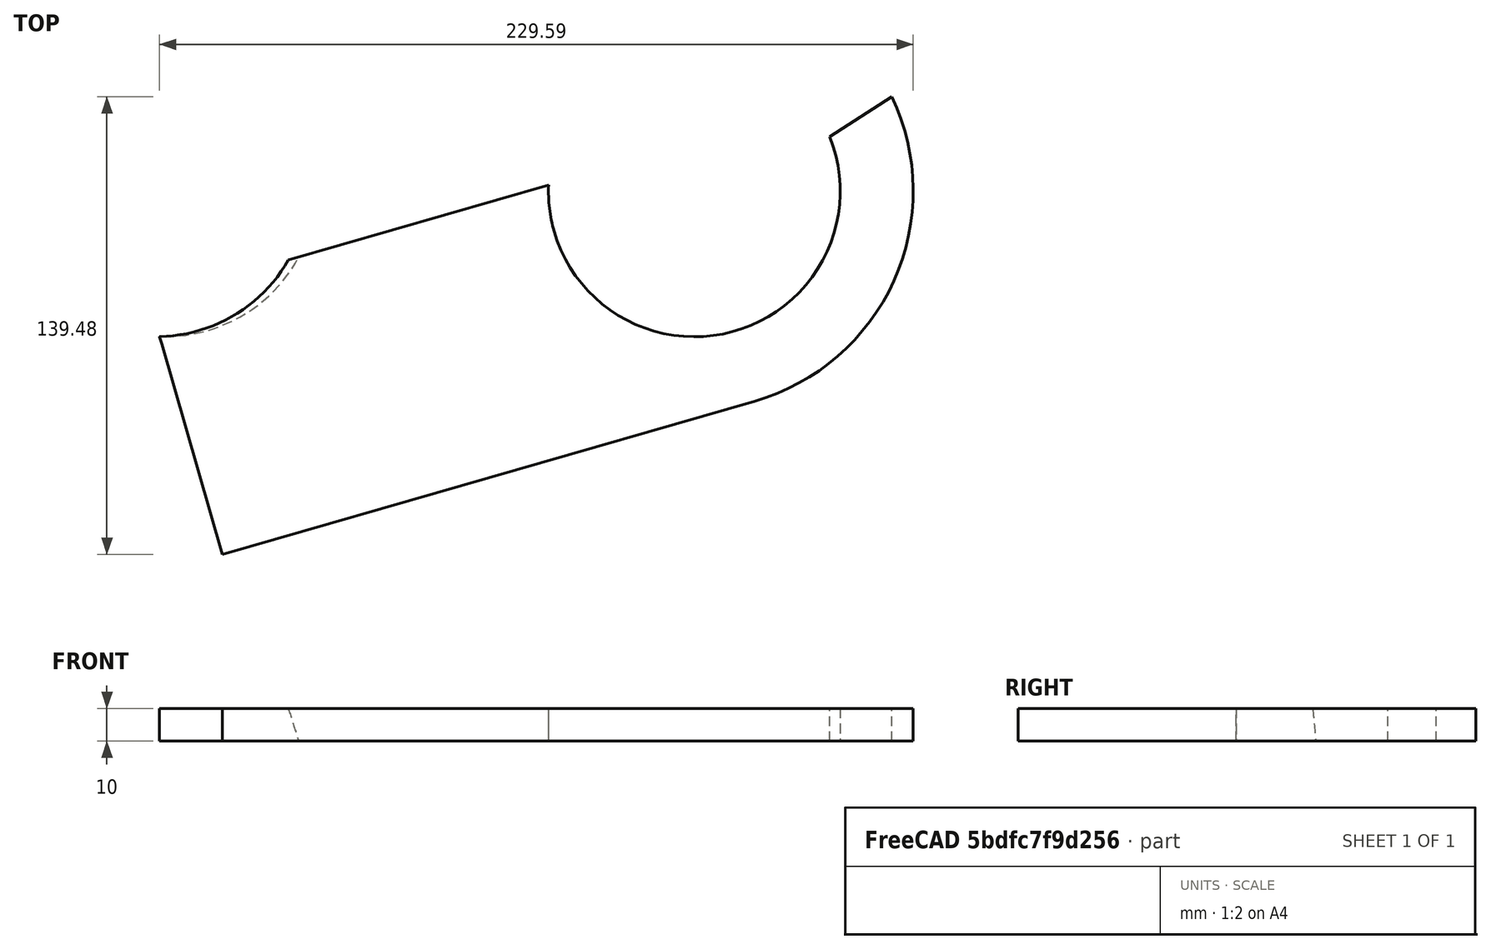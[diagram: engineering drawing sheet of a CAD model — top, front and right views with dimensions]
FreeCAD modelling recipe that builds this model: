
FCSTD DOCUMENT  (FreeCAD 1.0R39109 (Git))
Label: Tail_Hinge_Outer
License: All rights reserved
LicenseURL: http://en.wikipedia.org/wiki/All_rights_reserved
objects: App::Link×3, Spreadsheet::Sheet×1, Part::Cylinder×1, Part::Cut×1, App::Part×1
note: 2 computed .brp shape members not serialized (recipe doc carries the construction recipe); baked Part::Feature solids carry a one-line shape summary decoded from their .brp
EXTERNAL_REF file=Tail_Hinge_Outer_Pipe.FCStd obj=Tube
EXTERNAL_REF file=Tail_Hinge_Outer_Pipe_Cover.FCStd obj=PadBody
EXTERNAL_REF file=../../../Master_of_Puppets.FCStd obj=Alternator
EXTERNAL_REF file=../../../Master_of_Puppets.FCStd obj=HighEndStop
EXTERNAL_REF file=../../../Master_of_Puppets.FCStd obj=LowEndStop
EXTERNAL_REF file=../../../Master_of_Puppets.FCStd obj=Spreadsheet
EXTERNAL_REF file=../../../Master_of_Puppets.FCStd obj=Tail
EXTERNAL_REF file=../../Stops/Tail_Stop_LowEnd.FCStd obj=PocketBody

FEATURE [App::Link] Link  label="Pipe"
  LinkedObject = -> <external Tail_Hinge_Outer_Pipe.FCStd>#Tube
FEATURE [App::Link] Link001  label="Outer_Pipe_Cover"
  LinkPlacement = pos=(0,0,225.987) rot=(0,0,1;0rad)
  LinkedObject = -> <external Tail_Hinge_Outer_Pipe_Cover.FCStd>#PadBody
  Placement = pos=(0,0,225.987) rot=(0,0,1;0rad)
  expr: .Placement.Base.z = Spreadsheet.HingeOuterPipeCoverZ
FEATURE [Spreadsheet::Sheet] Spreadsheet
  cells = A1='Inputs; A2='HingeOuterPipeLength; B2(HingeOuterPipeLength)==Master_of_Puppets#Tail.HingeOuterPipeLength; A3='FlatMetalThickness; B3(FlatMetalThickness)==Master_of_Puppets#Spreadsheet.FlatMetalThickness; A4='TailBoomTriangularBraceWidth; B4(TailBoomTriangularBraceWidth)==Master_of_Puppets#Tail.TailBoomTriangularBraceWidth; A5='LowEndStopPlacement; B5(LowEndStopPlacement)==Master_of_Puppets#LowEndStop.LowEndStopPlacement; A6='YawPipeRadius; B6(YawPipeRadius)==Master_of_Puppets#Alternator.YawPipeRadius; A7='YawPipeLength; B7(YawPipeLength)==Master_of_Puppets#HighEndStop.YawPipeLength; A8='OuterTailHingePlacement; B8(OuterTailHingePlacement)==Master_of_Puppets#Tail.OuterTailHingePlacement; A9='TailAssemblyPlacement; B9(TailAssemblyPlacement)==Master_of_Puppets#HighEndStop.TailAssemblyPlacement; A10='Placement; A11='HingeOuterPipeCoverZ; B11(HingeOuterPipeCoverZ)==HingeOuterPipeLength; A12='YawBearingCylinderPlacement; B12(YawBearingCylinderPlacement)==minvert(OuterTailHingePlacement) * minvert(TailAssemblyPlacement)
FEATURE [App::Link] Link002  label="Stop_LowEnd"
  LinkPlacement = pos=(0,0,155.983) rot=(0,0,-1;1.29045rad)
  LinkedObject = -> <external ../../Stops/Tail_Stop_LowEnd.FCStd>#PocketBody
  Placement = pos=(0,0,155.983) rot=(0,0,-1;1.29045rad)
  expr: Placement = Spreadsheet.LowEndStopPlacement
FEATURE [Part::Cylinder] Cylinder  label="YawBearing_Cylinder"
  Angle = 360
  AttacherType = Attacher::AttachEngine3D
  FirstAngle = 0
  Height = 405
  Placement = pos=(-79.4354,1.24e-14,-150.518) rot=(-0.130416,-0.04112,0.990606;2.53612rad)
  Radius = 44.45
  SecondAngle = 0
  expr: Height = Spreadsheet.YawPipeLength
  expr: Placement = Spreadsheet.YawBearingCylinderPlacement
  expr: Radius = Spreadsheet.YawPipeRadius
FEATURE [Part::Cut] Cut  label="Tail_Stop_LowEnd"
  Base = -> Link002
  Openafpm_Flat = true
  Tool = -> Cylinder
FEATURE [App::Part] Part  label="Tail_Hinge_Outer"
  Group = -> [Link,Link001,Link002,Cylinder,Cut]
  Origin = -> Origin

RESOLVED EXTERNAL PARTS (link-assembly join: the EXTERNAL_REF files above that resolve inside this repo's crawl, each included once):
---- part ../../../Master_of_Puppets.FCStd = doc fcstd_6404554055c4 (61625 chars; too large to inline — full recipe in that document) ----
---- part ../../Stops/Tail_Stop_LowEnd.FCStd = doc fcstd_18032a887a06 ----
FCSTD DOCUMENT  (FreeCAD 0.21R33675 (Git))
Label: Tail_Stop_LowEnd
License: All rights reserved
LicenseURL: http://en.wikipedia.org/wiki/All_rights_reserved
objects: Sketcher::SketchObject×1, PartDesign::Pad×1, Spreadsheet::Sheet×1, PartDesign::Body×1
note: 4 computed .brp shape members not serialized (recipe doc carries the construction recipe); baked Part::Feature solids carry a one-line shape summary decoded from their .brp
EXTERNAL_REF file=../../Master_of_Puppets.FCStd obj=LowEndStop
EXTERNAL_REF file=../../Master_of_Puppets.FCStd obj=Spreadsheet
EXTERNAL_REF file=../../Master_of_Puppets.FCStd obj=Tail

FEATURE [Sketcher::SketchObject] Sketch
  FullyConstrained = true
  MapMode = 5
  Support = -> [XY_Plane001]
  expr: Constraints[13] = Spreadsheet.InnerArcAngle
  expr: Constraints[14] = Spreadsheet.OuterArcAngle
  expr: Constraints[15] = Spreadsheet.LowEndStopWidth
  expr: Constraints[1] = Spreadsheet.LowEndStopLength
  expr: Constraints[24] = Spreadsheet.LowEndStopWidth
  expr: Constraints[25] = Spreadsheet.LowEndStopLength
  expr: Constraints[33] = Spreadsheet.LowEndStopYawBearingOverlap
  expr: Constraints[7] = Spreadsheet.HingeOuterPipeRadius
  sketch-geometry (12):
    g0: LineSegment StartX=0 StartY=0 StartZ=0 EndX=0 EndY=-198.64 EndZ=0
    g1: LineSegment StartX=66.675 StartY=-198.64 StartZ=0 EndX=66.675 EndY=0 EndZ=0
    g2: ArcOfCircle CenterX=0 CenterY=0 CenterZ=0 NormalX=0 NormalY=0 NormalZ=1 AngleXU=0 Radius=66.675 StartAngle=0 EndAngle=1.48304
    g3: Circle CenterX=0 CenterY=0 CenterZ=0 NormalX=0 NormalY=0 NormalZ=1 AngleXU=0 Radius=44.45
    g4: ArcOfCircle CenterX=0 CenterY=0 CenterZ=0 NormalX=0 NormalY=0 NormalZ=1 AngleXU=0 Radius=44.45 StartAngle=4.71239 EndAngle=7.71269
    g5: LineSegment StartX=6.25936 StartY=44.0071 StartZ=0 EndX=5.84395 EndY=66.4184 EndZ=0
    g6: LineSegment StartX=-8.2e-15 StartY=-198.64 StartZ=0 EndX=-8.2e-15 EndY=-44.45 EndZ=0
    g7: ArcOfCircle CenterX=0 CenterY=0 CenterZ=0 NormalX=0 NormalY=0 NormalZ=1 AngleXU=0 Radius=44.45 StartAngle=4.71239 EndAngle=10.9956
    g8: LineSegment StartX=-8.2e-15 StartY=-198.64 StartZ=0 EndX=66.675 EndY=-198.64 EndZ=0
    g9: LineSegment StartX=-8.2e-15 StartY=-198.64 StartZ=0 EndX=-14 EndY=-198.64 EndZ=0
    g10: LineSegment StartX=-14 StartY=-198.64 StartZ=0 EndX=-14 EndY=-42.1877 EndZ=0
    g11: ArcOfCircle CenterX=0 CenterY=0 CenterZ=0 NormalX=0 NormalY=0 NormalZ=1 AngleXU=0 Radius=44.45 StartAngle=4.39197 EndAngle=4.71239
  constraints (34):
    c: Vertical(g1)
    c: Distance(g0) = 198.64
    c: Coincident(g0,g-1)
    c: Coincident(g2,g0)
    c: Coincident(g2,g1)
    c: PointOnObject(g1,g-1)
    c: Coincident(g3,g2)
    c: Radius(g3) = 44.45
    c: PointOnObject(g4,g0)
    c: Coincident(g4,g2)
    c: PointOnObject(g4,g3)
    c: Coincident(g5,g4)
    c: Coincident(g5,g2)
    c: Angle(g4) = 3.00031
    c: Angle(g2) = 1.48304
    c: DistanceX(g-2,g1) = 66.675
    c: Vertical(g6)
    c: Vertical(g0)
    c: Coincident(g7,g2)
    c: Coincident(g7,g4)
    c: Coincident(g7,g6)
    c: Coincident(g8,g6)
    c: Coincident(g8,g1)
    c: Horizontal(g8)
    c: DistanceX(g8,g8) = 66.675
    c: DistanceY(g6,g2) = 198.64
    c: Coincident(g9,g6)
    c: Horizontal(g9)
    c: Coincident(g10,g9)
    c: Vertical(g10)
    c: Coincident(g11,g2)
    c: Coincident(g11,g4)
    c: Coincident(g11,g10)
    c: DistanceX(g9,g9) = 14
FEATURE [PartDesign::Pad] Pad
  AllowMultiFace = false
  Direction = (0,0,1)
  Length = 10
  Length2 = 100
  Profile = -> Sketch
  Type = 0
  expr: Length = Spreadsheet.FlatMetalThickness
FEATURE [Spreadsheet::Sheet] Spreadsheet
  cells = A1='Inputs; A2='YawPipeDiameter; B2(YawPipeDiameter)==Master_of_Puppets#Spreadsheet.YawPipeDiameter; A3='FlatMetalThickness; B3(FlatMetalThickness)==Master_of_Puppets#Spreadsheet.FlatMetalThickness; A4='TailHingeJunctionFullWidth; B4(TailHingeJunctionFullWidth)==Master_of_Puppets#Tail.TailHingeJunctionFullWidth; A5='OuterTailHingeLowEndStopAngle; B5(OuterTailHingeLowEndStopAngle)==Master_of_Puppets#LowEndStop.LowEndStopAngle; A6='TailBoomTriangularBraceWidth; B6(TailBoomTriangularBraceWidth)==Master_of_Puppets#Tail.TailBoomTriangularBraceWidth; A7='TailAngle; B7(TailAngle)==Master_of_Puppets#Tail.TailAngle; A8='TailY; B8(TailBoomY)==Master_of_Puppets#Tail.TailY; A9='LowEndStopLength; B9(LowEndStopLength)==Master_of_Puppets#LowEndStop.LowEndStopLength; A10='RotorDiskRadius; B10(RotorDiskRadius)==Master_of_Puppets#Spreadsheet.RotorDiskRadius; A11='OuterLowEndStopWidth; B11(OuterLowEndStopWidth)==Master_of_Puppets#LowEndStop.OuterLowEndStopWidth; A12='LowEndStopYawBearingOverlap; B12(LowEndStopYawBearingOverlap)==Master_of_Puppets#LowEndStop.LowEndStopYawBearingOverlap; A13='LowEndStopWidth; B13(LowEndStopWidth)==Master_of_Puppets#LowEndStop.LowEndStopWidth; A14='HingeOuterPipeRadius; B14(HingeOuterPipeRadius)==Master_of_Puppets#Tail.HingeOuterPipeRadius; A15='Calculated; A16='HalfTriangularBraceThickness; B16(HalfTriangularBraceThickness)==FlatMetalThickness / 2; A17='TriangularBraceOffsetFactor; B17(TriangularBraceOffsetFactor)=-1; C17='Set TriangularBraceOffsetFactor to 1 to extend low end stop underneath boom & above boom support; A18='Inner Arc Angle; C18='Outer Arc Angle; A19='InnerTriangularBraceAngleOffset; B19(InnerTriangularBraceAngleOffset)==HalfTriangularBraceThickness / HingeOuterPipeRadius * 180 / pi * 1 deg * TriangularBraceOffsetFactor; C19='OuterTriangularBraceAngleOffset; D19(OuterTriangularBraceAngleOffset)==HalfTriangularBraceThickness / LowEndStopWidth * 180 / pi * 1 deg * TriangularBraceOffsetFactor; A20='InnerTailBoomYAngleOffset; B20(InnerTailBoomYAngleOffset)==TailBoomY / HingeOuterPipeRadius * 180 / pi * 1 deg; C20='OuterTailBoomYAngleOffset; D20(OuterTailBoomYAngleOffset)==TailBoomY / LowEndStopWidth * 180 / pi * 1 deg; C21='TailBoomRotationYOffset; D21(TailBoomRotationYOffset)==sin(TailAngle) * OuterLowEndStopWidth; A22='InnerAngle; B22(InnerAngle)==OuterTailHingeLowEndStopAngle + InnerTriangularBraceAngleOffset + InnerTailBoomYAngleOffset; C22='TailBoomRotationAngleOffset; D22(TailBoomRotationAngleOffset)==TailBoomRotationYOffset / LowEndStopWidth * 180 / pi * 1 deg; A23='InnerArcAngle; B23(InnerArcAngle)==90 deg + InnerAngle; C23='OuterArcAngle; D23(OuterArcAngle)==OuterTailHingeLowEndStopAngle + OuterTriangularBraceAngleOffset + OuterTailBoomYAngleOffset + TailBoomRotationAngleOffset
FEATURE [PartDesign::Body] PocketBody  label="Tail_Stop_LowEnd"
  Group = -> [Sketch,Pad]
  Origin = -> Origin001
  Tip = -> Pad
---- part Tail_Hinge_Outer_Pipe_Cover.FCStd = doc fcstd_64ac9c9964c2 ----
FCSTD DOCUMENT  (FreeCAD 0.21R33675 (Git))
Label: Tail_Hinge_Outer_Pipe_Cover
License: All rights reserved
LicenseURL: http://en.wikipedia.org/wiki/All_rights_reserved
objects: Sketcher::SketchObject×1, PartDesign::Pad×1, Spreadsheet::Sheet×1, PartDesign::Body×1
note: 4 computed .brp shape members not serialized (recipe doc carries the construction recipe); baked Part::Feature solids carry a one-line shape summary decoded from their .brp
EXTERNAL_REF file=../../../Master_of_Puppets.FCStd obj=Spreadsheet
EXTERNAL_REF file=../../../Master_of_Puppets.FCStd obj=Tail

FEATURE [Sketcher::SketchObject] Sketch
  FullyConstrained = true
  MapMode = 5
  Support = -> [XY_Plane001]
  expr: Constraints[1] = Spreadsheet.HingeOuterPipeRadius
  sketch-geometry (1):
    g0: Circle CenterX=0 CenterY=0 CenterZ=0 NormalX=0 NormalY=0 NormalZ=1 AngleXU=0 Radius=24.15
  constraints (2):
    c: Coincident(g0,g-1)
    c: Radius(g0) = 24.15
FEATURE [PartDesign::Pad] Pad
  AllowMultiFace = false
  Direction = (0,0,1)
  Length = 10
  Length2 = 100
  Profile = -> Sketch
  Type = 0
  expr: Length = Spreadsheet.FlatMetalThickness
FEATURE [Spreadsheet::Sheet] Spreadsheet
  cells = A1='Inputs; A2='HingeOuterPipeRadius; B2(HingeOuterPipeRadius)==Master_of_Puppets#Tail.HingeOuterPipeRadius; A3='FlatMetalThickness; B3(FlatMetalThickness)==Master_of_Puppets#Spreadsheet.FlatMetalThickness
FEATURE [PartDesign::Body] PadBody  label="Tail_Hinge_Outer_Pipe_Cover"
  Group = -> [Sketch,Pad]
  Openafpm_Flat = true
  Origin = -> Origin001
  Tip = -> Pad
